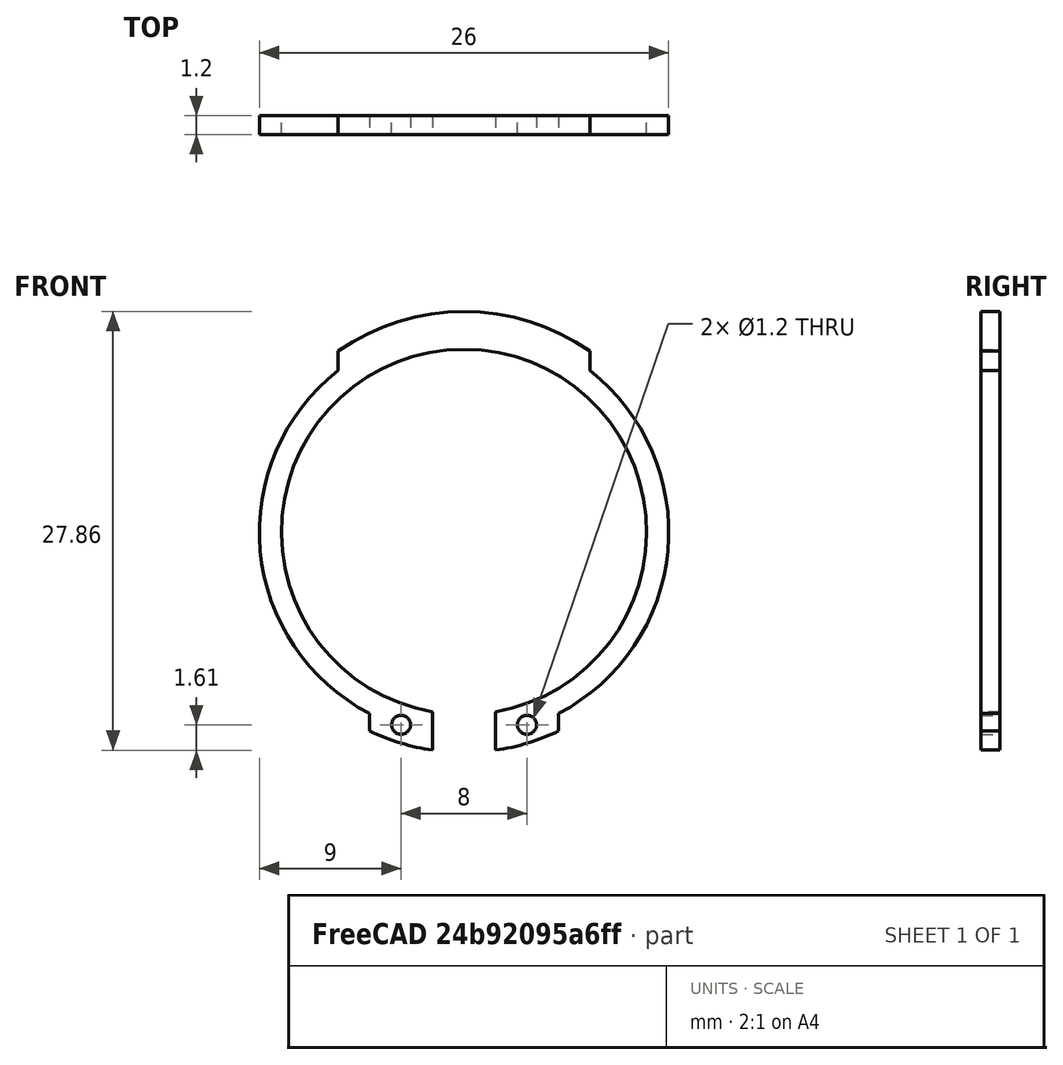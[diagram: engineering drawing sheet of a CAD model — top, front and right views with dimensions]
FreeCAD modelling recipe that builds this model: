
FCSTD DOCUMENT  (FreeCAD 0.20R29126 (Git))
Label: electric-motor-locking-ring
License: All rights reserved
LicenseURL: http://en.wikipedia.org/wiki/All_rights_reserved
objects: Sketcher::SketchObject×1, PartDesign::Pad×1, PartDesign::Body×1
note: 4 computed .brp shape members not serialized (recipe doc carries the construction recipe); baked Part::Feature solids carry a one-line shape summary decoded from their .brp

FEATURE [Sketcher::SketchObject] Sketch
  FullyConstrained = true
  MapMode = 5
  Placement = pos=(0,0,0) rot=(1,0,0;1.5708rad)
  Support = -> [XZ_Plane]
  sketch-geometry (14):
    g0: ArcOfCircle CenterX=0 CenterY=0 CenterZ=0 NormalX=0 NormalY=0 NormalZ=1 AngleXU=0 Radius=11.6 StartAngle=4.88567 EndAngle=10.8223
    g1: ArcOfCircle CenterX=0 CenterY=0 CenterZ=0 NormalX=0 NormalY=0 NormalZ=1 AngleXU=0 Radius=14 StartAngle=4.85574 EndAngle=5.1553
    g2: LineSegment StartX=-2 StartY=-11.4263 StartZ=0 EndX=-2 EndY=-13.8564 EndZ=0
    g3: LineSegment StartX=2 StartY=-11.4263 StartZ=0 EndX=2 EndY=-13.8564 EndZ=0
    g4: ArcOfCircle CenterX=0 CenterY=0 CenterZ=0 NormalX=0 NormalY=0 NormalZ=1 AngleXU=0 Radius=13 StartAngle=5.19212 EndAngle=7.19111
    g5: LineSegment StartX=-6 StartY=-12.6491 StartZ=0 EndX=-6 EndY=-11.5326 EndZ=0
    g6: LineSegment StartX=6 StartY=-11.5326 StartZ=0 EndX=6 EndY=-12.6491 EndZ=0
    g7: LineSegment StartX=-8 StartY=10.247 StartZ=0 EndX=-8 EndY=11.4891 EndZ=0
    g8: LineSegment StartX=8 StartY=10.247 StartZ=0 EndX=8 EndY=11.4891 EndZ=0
    g9: ArcOfCircle CenterX=0 CenterY=0 CenterZ=0 NormalX=0 NormalY=0 NormalZ=1 AngleXU=0 Radius=14 StartAngle=0.962551 EndAngle=2.17904
    g10: ArcOfCircle CenterX=0 CenterY=0 CenterZ=0 NormalX=0 NormalY=0 NormalZ=1 AngleXU=0 Radius=14 StartAngle=4.26948 EndAngle=4.56904
    g11: ArcOfCircle CenterX=0 CenterY=0 CenterZ=0 NormalX=0 NormalY=0 NormalZ=1 AngleXU=0 Radius=13 StartAngle=2.23367 EndAngle=4.23266
    g12: Circle CenterX=-4 CenterY=-12.25 CenterZ=0 NormalX=0 NormalY=0 NormalZ=1 AngleXU=0 Radius=0.6
    g13: Circle CenterX=4 CenterY=-12.25 CenterZ=0 NormalX=0 NormalY=0 NormalZ=1 AngleXU=0 Radius=0.6
  constraints (40):
    c: Coincident(g0,g-1)
    c: Coincident(g1,g0)
    c: Vertical(g2)
    c: Vertical(g3)
    c: Coincident(g4,g0)
    c: Vertical(g5)
    c: Vertical(g6)
    c: Coincident(g0,g2)
    c: Coincident(g0,g3)
    c: Coincident(g10,g2)
    c: Coincident(g1,g3)
    c: Coincident(g11,g5)
    c: Coincident(g4,g6)
    c: PointOnObject(g7,g1)
    c: Vertical(g8)
    c: Vertical(g7)
    c: Coincident(g1,g6)
    c: Coincident(g9,g8)
    c: Coincident(g1,g9)
    c: PointOnObject(g9,g7)
    c: PointOnObject(g10,g5)
    c: Coincident(g9,g10)
    c: Equal(g4,g11)
    c: Coincident(g4,g8)
    c: Coincident(g11,g7)
    c: Coincident(g4,g11)
    c: Symmetric(g2,g1,g-2)
    c: Symmetric(g1,g5,g-2)
    c: Symmetric(g7,g8,g-2)
    c: Radius(g0) = 11.6
    c: Equal(g12,g13)
    c: Radius(g13) = 0.6
    c: Symmetric(g12,g13,g-2)
    c: DistanceX(g-1,g13) = 4
    c: DistanceX(g2,g1) = 4
    c: Radius(g4) = 13
    c: DistanceY(g12,g0) = 12.25
    c: Radius(g9) = 14
    c: DistanceX(g7,g4) = 16
    c: DistanceX(g5,g1) = 12
FEATURE [PartDesign::Pad] Pad
  Direction = (0,-1,2e-16)
  Length = 1.2
  Length2 = 10
  Placement = pos=(0,0,0) rot=(1,0,0;1.5708rad)
  Profile = -> Sketch
  ReferenceAxis = -> Sketch [N_Axis]
  Type = 0
FEATURE [PartDesign::Body] Body
  Group = -> [Sketch,Pad]
  Origin = -> Origin
  Tip = -> Pad
